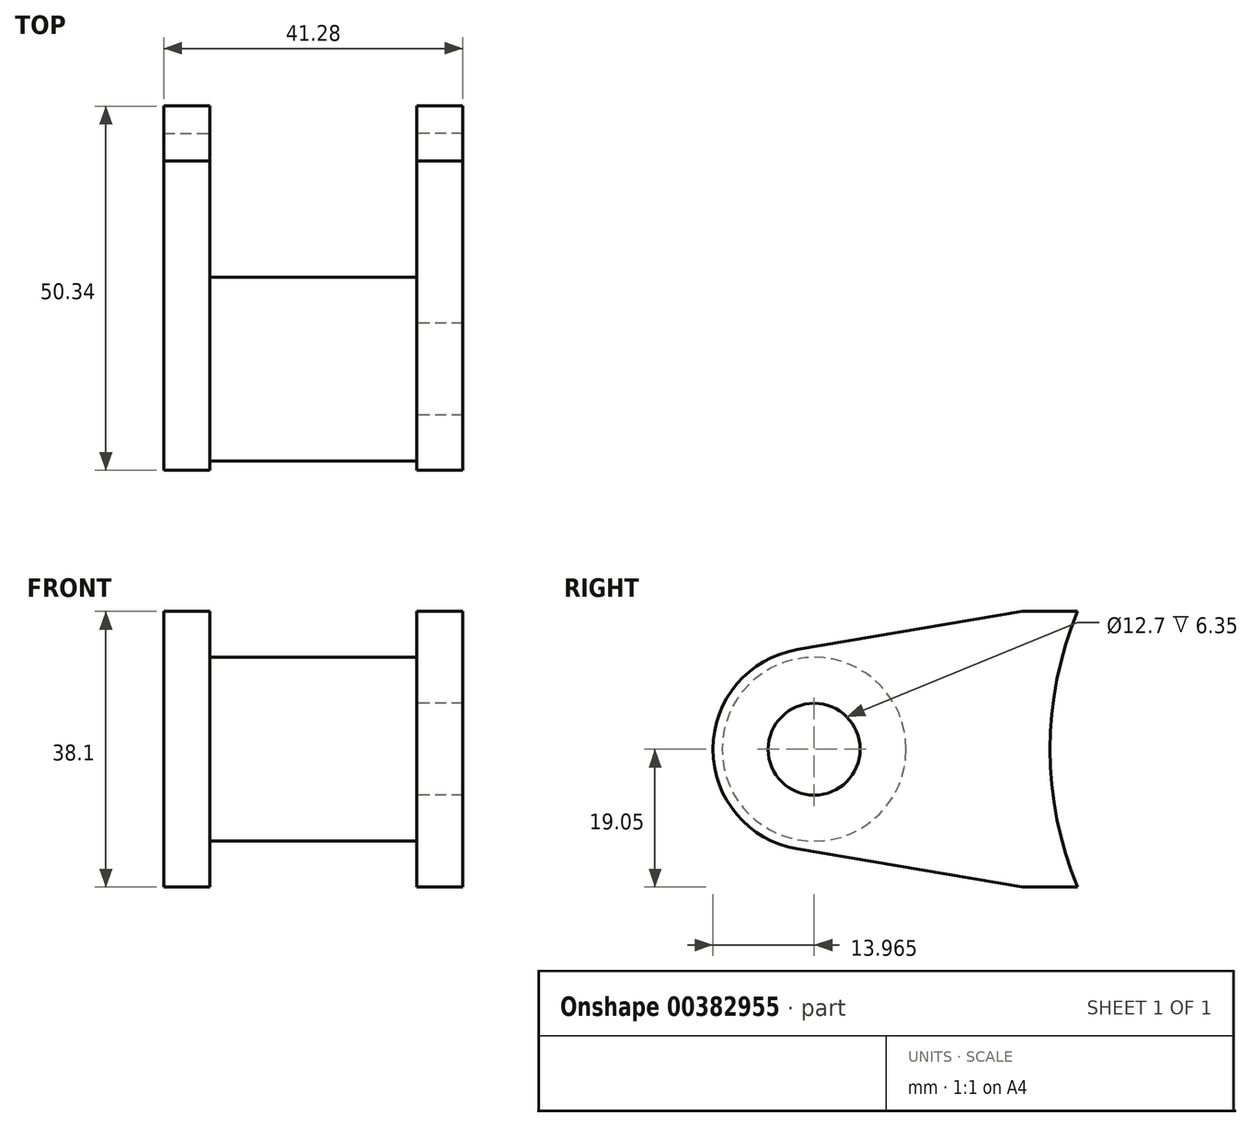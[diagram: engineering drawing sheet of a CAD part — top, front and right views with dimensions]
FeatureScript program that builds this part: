
annotation { "Feature Type Name" : "Feature", "Feature Type Description" : "" }
export const myFeature = defineFeature(function(context is Context, id is Id, definition is map)
    precondition{}
    {
        {
            var Q0;
            Q0=qCreatedBy(makeId("Right.planeOp"),FACE);
            var sketch = newSketch(context, id + "F0", { "sketchPlane" : qUnion([Q0])});
            skCircle(sketch, "E0", {"center": v(-25.61, 0) * mm, "radius": 12.7 * mm});
            skSolve(sketch);
        }
        {
            var Q0;
            Q0=makeQuery(id+"F0.imprint","IMPRINT",FACE,{"disambiguationData":[TD([[makeQuery(id+"F0.imprint","IMPRINT",EDGE,{"derivedFrom":sQuery(id+"F0.wireOp",EDGE,"E0")}),1.0]])]});
            extrude(context, id + "F1", {"entities" : qUnion([Q0]), "endBound" : BoundingType.SYMMETRIC, "depth" : 28.57 * mm});
        }
        {
            var Q0;
            Q0=makeQuery(id+"F1.opExtrude","CAP_FACE",FACE,{"disambiguationData":[OSD([sQuery(id+"F0.wireOp",EDGE,"E0")])],"isStart":false});
            var sketch = newSketch(context, id + "F2", { "sketchPlane" : qUnion([Q0])});
            skLineSegment(sketch, "E1.bottom", {"start": v(3.14, 19.05) * mm, "end": v(10.76, 19.05) * mm});
            skLineSegment(sketch, "E1.top", {"start": v(3.14, -19.05) * mm, "end": v(10.76, -19.05) * mm});
            skLineSegment(sketch, "E1.left", {"start": v(3.14, 19.05) * mm, "end": v(3.14, -19.05) * mm});
            skLineSegment(sketch, "E1.right", {"start": v(10.76, 19.05) * mm, "end": v(10.76, -19.05) * mm});
            skPoint(sketch, "E1.middle", {"position": v(6.95, 0) * mm});
            skCircle(sketch, "E2", {"center": v(-25.61, 0) * mm, "radius": 13.97 * mm});
            skLineSegment(sketch, "E3", {"start": v(3.14, 19.05) * mm, "end": v(-27.95, 13.77) * mm});
            skLineSegment(sketch, "E4", {"start": v(3.14, -19.05) * mm, "end": v(-27.95, -13.77) * mm});
            skArc(sketch, "E5", {"start": v(10.76, 19.05) * mm, "mid": v(6.95, 0) * mm, "end": v(10.76, -19.05) * mm});
            skSolve(sketch);
        }
        {
            var Q0;
            Q0=makeQuery(id+"F2.imprint","IMPRINT",FACE,{"disambiguationData":[TD([[makeQuery(id+"F2.imprint","IMPRINT",EDGE,{"derivedFrom":sQuery(id+"F2.wireOp",EDGE,"E1.bottom")}),-1.0]])]});
            var Q1;
            Q1=makeQuery(id+"F2.imprint","IMPRINT",FACE,{"disambiguationData":[TD([[makeQuery(id+"F2.imprint","IMPRINT",EDGE,{"derivedFrom":sQuery(id+"F2.wireOp",EDGE,"E1.left")}),-1.0]])]});
            var Q2;
            Q2=makeQuery(id+"F2.imprint","IMPRINT",FACE,{"disambiguationData":[TD([[makeQuery(id+"F2.imprint","IMPRINT",EDGE,{"derivedFrom":makeQuery(id+"F1.opExtrude","CAP_EDGE",EDGE,{"disambiguationData":[OSD([sQuery(id+"F0.wireOp",EDGE,"E0")])],"isStart":false})}),-1.0]])]});
            var Q3;
            Q3=makeQuery(id+"F2.imprint","IMPRINT",FACE,{"disambiguationData":[TD([[makeQuery(id+"F2.imprint","IMPRINT",EDGE,{"derivedFrom":makeQuery(id+"F1.opExtrude","CAP_EDGE",EDGE,{"disambiguationData":[OSD([sQuery(id+"F0.wireOp",EDGE,"E0")])],"isStart":false})}),1.0]])]});
            extrude(context, id + "F3", {"entities" : qUnion([Q0, Q1, Q2, Q3]), "operationType" : NewBodyOperationType.ADD, "depth" : 6.35 * mm});
        }
        {
            var Q0;
            Q0=makeQuery(id+"F1.opExtrude","SWEPT_BODY",BODY,{"disambiguationData":[OSD([sQuery(id+"F0.wireOp",EDGE,"E0")])]});
            var Q1;
            Q1=qCreatedBy(makeId("Right.planeOp"),FACE);
            mirror(context, id + "F4", {"operationType" : NewBodyOperationType.ADD, "entities" : qUnion([Q0]), "mirrorPlane" : qUnion([Q1])});
        }
        {
            var Q0;
            Q0=sQuery(id+"F2.wireOp",VERTEX,"E2.center");
            var Q1;
            Q1=makeQuery(id+"F1.opExtrude","SWEPT_BODY",BODY,{"disambiguationData":[OSD([sQuery(id+"F0.wireOp",EDGE,"E0")])]});
            hole(context, id + "F5", {"style" : HoleStyle.SIMPLE, "endStyle" : HoleEndStyle.BLIND, "oppositeDirection" : true, "holeDiameter" : 12.7 * mm, "holeDepth" : 12.7 * mm, "isTappedThrough" : true, "tappedDepth" : 12.7 * mm, "tapClearance" : 3, "startFromSketch" : true, "locations" : qUnion([Q0]), "scope" : qUnion([Q1])});
        }
    });
